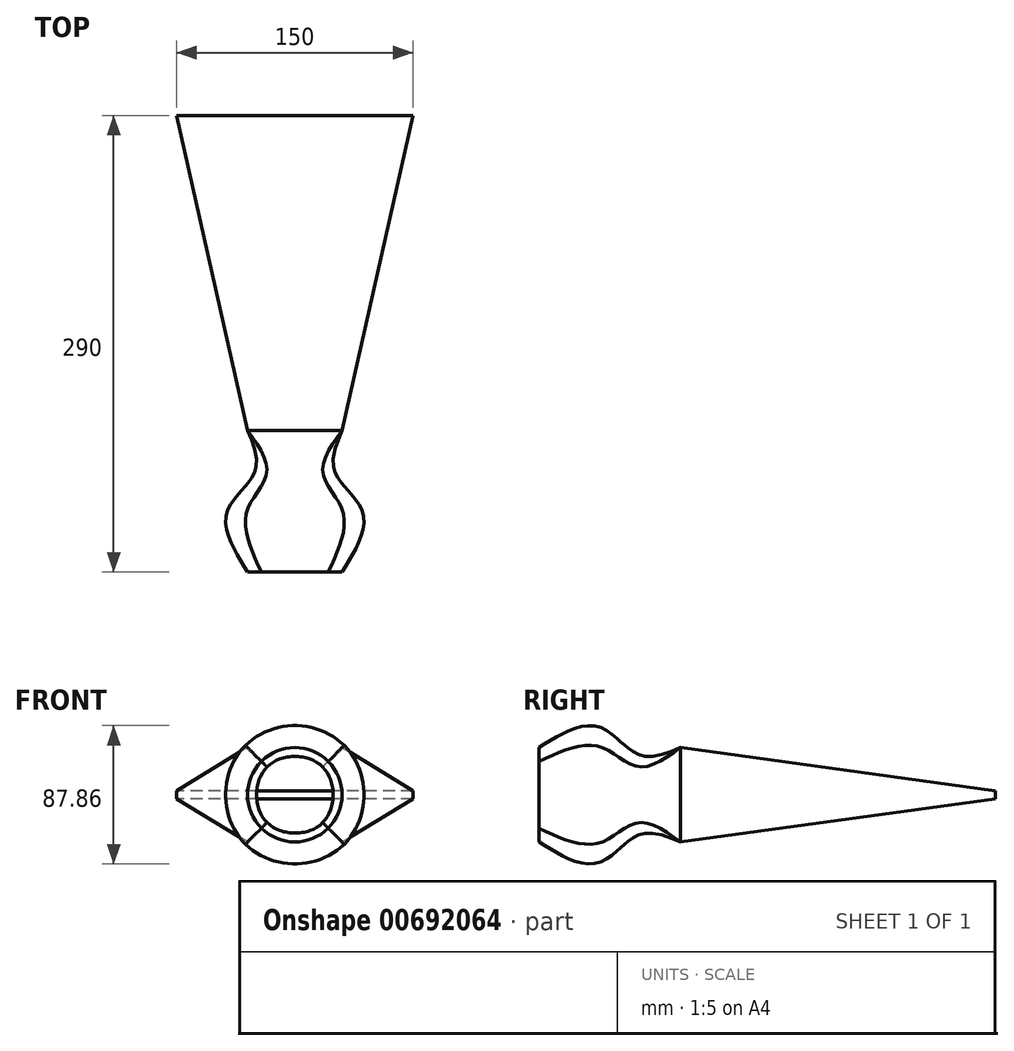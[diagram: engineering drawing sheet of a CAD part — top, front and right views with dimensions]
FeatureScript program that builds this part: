
annotation { "Feature Type Name" : "Feature", "Feature Type Description" : "" }
export const myFeature = defineFeature(function(context is Context, id is Id, definition is map)
    precondition{}
    {
        {
            var Q0;
            Q0=qCreatedBy(makeId("Front.planeOp"),FACE);
            cPlane(context, id + "F0", {"entities" : qUnion([Q0]), "cplaneType" : CPlaneType.OFFSET, "offset" : 25 * mm, "width" : 152.4 * mm, "height" : 152.4 * mm});
        }
        {
            var Q0;
            Q0=qCreatedBy(id+"F0.planeOp",FACE);
            cPlane(context, id + "F1", {"entities" : qUnion([Q0]), "cplaneType" : CPlaneType.OFFSET, "offset" : 25 * mm, "width" : 152.4 * mm, "height" : 152.4 * mm});
        }
        {
            var Q0;
            Q0=qCreatedBy(id+"F1.planeOp",FACE);
            cPlane(context, id + "F2", {"entities" : qUnion([Q0]), "cplaneType" : CPlaneType.OFFSET, "offset" : 40 * mm, "width" : 152.4 * mm, "height" : 152.4 * mm});
        }
        {
            var Q0;
            Q0=qCreatedBy(makeId("Front.planeOp"),FACE);
            var sketch = newSketch(context, id + "F3", { "sketchPlane" : qUnion([Q0])});
            skLineSegment(sketch, "E0.bottom", {"start": v(30, -30) * mm, "end": v(-30, -30) * mm});
            skLineSegment(sketch, "E0.top", {"start": v(30, 30) * mm, "end": v(-30, 30) * mm});
            skLineSegment(sketch, "E0.left", {"start": v(30, -30) * mm, "end": v(30, 30) * mm});
            skLineSegment(sketch, "E0.right", {"start": v(-30, -30) * mm, "end": v(-30, 30) * mm});
            skPoint(sketch, "E0.middle", {"position": v(0, 0) * mm});
            skSolve(sketch);
        }
        {
            var Q0;
            Q0=qCreatedBy(id+"F0.planeOp",FACE);
            var sketch = newSketch(context, id + "F4", { "sketchPlane" : qUnion([Q0])});
            skCircle(sketch, "E1", {"center": v(0, 0) * mm, "radius": 25 * mm});
            skSolve(sketch);
        }
        {
            var Q0;
            Q0=qCreatedBy(id+"F1.planeOp",FACE);
            var sketch = newSketch(context, id + "F5", { "sketchPlane" : qUnion([Q0])});
            skCircle(sketch, "E2", {"center": v(0, 0) * mm, "radius": 42.43 * mm});
            skSolve(sketch);
        }
        {
            var Q0;
            Q0=qCreatedBy(id+"F2.planeOp",FACE);
            var sketch = newSketch(context, id + "F6", { "sketchPlane" : qUnion([Q0])});
            skCircle(sketch, "E3", {"center": v(0, 0) * mm, "radius": 30 * mm});
            skSolve(sketch);
        }
        {
            var Q0;
            Q0=makeQuery(id+"F6.imprint","IMPRINT",FACE,{"disambiguationData":[TD([[makeQuery(id+"F6.imprint","IMPRINT",EDGE,{"derivedFrom":sQuery(id+"F6.wireOp",EDGE,"E3")}),1.0]])]});
            var Q1;
            Q1=sQuery(id+"F5.wireOp",EDGE,"E2");
            var Q2;
            Q2=sQuery(id+"F4.wireOp",EDGE,"E1");
            var Q3;
            Q3=makeQuery(id+"F3.imprint","IMPRINT",FACE,{"disambiguationData":[TD([[makeQuery(id+"F3.imprint","IMPRINT",EDGE,{"derivedFrom":sQuery(id+"F3.wireOp",EDGE,"E0.bottom")}),-1.0]])]});
            loft(context, id + "F7", {"bodyType" : ToolBodyType.SURFACE, "wireProfilesArray" : [{ "wireProfileEntities" : qUnion([Q0]) }, { "wireProfileEntities" : qUnion([Q1]) }, { "wireProfileEntities" : qUnion([Q2]) }, { "wireProfileEntities" : qUnion([Q3]) }]});
        }
        {
            var Q0;
            Q0=qCreatedBy(makeId("Front.planeOp"),FACE);
            cPlane(context, id + "F8", {"entities" : qUnion([Q0]), "cplaneType" : CPlaneType.OFFSET, "offset" : 200 * mm, "oppositeDirection" : true, "width" : 152.4 * mm, "height" : 152.4 * mm});
        }
        {
            var Q0;
            Q0=qCreatedBy(id+"F8.planeOp",FACE);
            var sketch = newSketch(context, id + "F9", { "sketchPlane" : qUnion([Q0])});
            skLineSegment(sketch, "E4.bottom", {"start": v(75, 2.5) * mm, "end": v(-75, 2.5) * mm});
            skLineSegment(sketch, "E4.top", {"start": v(75, -2.5) * mm, "end": v(-75, -2.5) * mm});
            skLineSegment(sketch, "E4.left", {"start": v(75, 2.5) * mm, "end": v(75, -2.5) * mm});
            skLineSegment(sketch, "E4.right", {"start": v(-75, 2.5) * mm, "end": v(-75, -2.5) * mm});
            skPoint(sketch, "E4.middle", {"position": v(0, 0) * mm});
            skSolve(sketch);
        }
        {
            var Q0;
            Q0 = qConstructionFilter(qBodyType(qCreatedBy(id + "F3" ,EDGE), BodyType.WIRE), ConstructionObject.NO);
            var Q1;
            Q1 = qConstructionFilter(qBodyType(qCreatedBy(id + "F9" ,EDGE), BodyType.WIRE), ConstructionObject.NO);
            loft(context, id + "F10", {"bodyType" : ToolBodyType.SURFACE, "wireProfilesArray" : [{ "wireProfileEntities" : qUnion([Q0]) }, { "wireProfileEntities" : qUnion([Q1]) }]});
        }
    });
